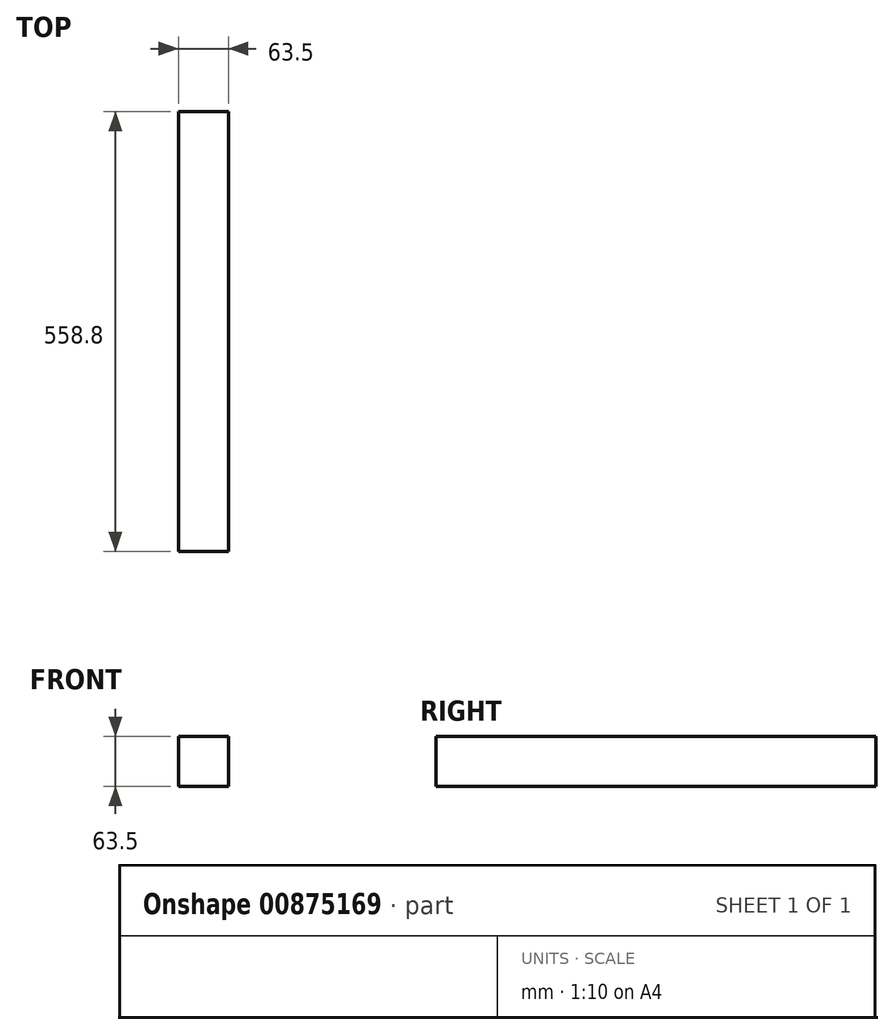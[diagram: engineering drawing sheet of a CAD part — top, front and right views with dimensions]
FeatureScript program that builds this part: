
annotation { "Feature Type Name" : "Feature", "Feature Type Description" : "" }
export const myFeature = defineFeature(function(context is Context, id is Id, definition is map)
    precondition{}
    {
        {
            var Q0;
            Q0=qCreatedBy(makeId("Front.planeOp"),FACE);
            var sketch = newSketch(context, id + "F0", { "sketchPlane" : qUnion([Q0])});
            skLineSegment(sketch, "E0.bottom", {"start": v(-164.57, 68.12) * mm, "end": v(-101.07, 68.12) * mm});
            skLineSegment(sketch, "E0.top", {"start": v(-164.57, 4.62) * mm, "end": v(-101.07, 4.62) * mm});
            skLineSegment(sketch, "E0.left", {"start": v(-164.57, 68.12) * mm, "end": v(-164.57, 4.62) * mm});
            skLineSegment(sketch, "E0.right", {"start": v(-101.07, 68.12) * mm, "end": v(-101.07, 4.62) * mm});
            skSolve(sketch);
        }
        {
            var Q0;
            Q0=makeQuery(id+"F0.imprint","IMPRINT",FACE,{"disambiguationData":[TD([[makeQuery(id+"F0.imprint","IMPRINT",EDGE,{"derivedFrom":sQuery(id+"F0.wireOp",EDGE,"E0.bottom")}),-1.0]])]});
            extrude(context, id + "F1", {"entities" : qUnion([Q0]), "depth" : 1498.6 * mm, "offsetDistance" : 25.4 * mm});
        }
        {
            var Q0;
            Q0=makeQuery(id+"F1.opExtrude","CAP_FACE",FACE,{"disambiguationData":[OSD([sQuery(id+"F0.wireOp",EDGE,"E0.bottom"),sQuery(id+"F0.wireOp",EDGE,"E0.top"),sQuery(id+"F0.wireOp",EDGE,"E0.left"),sQuery(id+"F0.wireOp",EDGE,"E0.right")])],"isStart":true});
            extrude(context, id + "F2", {"entities" : qUnion([Q0]), "operationType" : NewBodyOperationType.REMOVE, "oppositeDirection" : true, "depth" : 1092.2 * mm, "offsetDistance" : 25.4 * mm});
        }
        {
            var Q0;
            Q0=makeQuery(id+"F2.boolean.opBoolean","COPY",FACE,{"derivedFrom":makeQuery(id+"F2.opExtrude","CAP_FACE",FACE,{"disambiguationData":[OSD([sQuery(id+"F0.wireOp",EDGE,"E0.bottom"),sQuery(id+"F0.wireOp",EDGE,"E0.top"),sQuery(id+"F0.wireOp",EDGE,"E0.left"),sQuery(id+"F0.wireOp",EDGE,"E0.right")])],"isStart":false})});
            extrude(context, id + "F3", {"entities" : qUnion([Q0]), "operationType" : NewBodyOperationType.REMOVE, "oppositeDirection" : true, "depth" : 203.2 * mm, "offsetDistance" : 25.4 * mm});
        }
        {
            var Q0;
            Q0=makeQuery(id+"F1.opExtrude","CAP_FACE",FACE,{"disambiguationData":[OSD([sQuery(id+"F0.wireOp",EDGE,"E0.bottom"),sQuery(id+"F0.wireOp",EDGE,"E0.top"),sQuery(id+"F0.wireOp",EDGE,"E0.left"),sQuery(id+"F0.wireOp",EDGE,"E0.right")])],"isStart":false});
            extrude(context, id + "F4", {"entities" : qUnion([Q0]), "operationType" : NewBodyOperationType.REMOVE, "oppositeDirection" : true, "depth" : 177.8 * mm, "offsetDistance" : 25.4 * mm});
        }
        {
            var Q0;
            Q0=makeQuery(id+"F3.boolean.opBoolean","COPY",FACE,{"derivedFrom":makeQuery(id+"F3.opExtrude","CAP_FACE",FACE,{"disambiguationData":[OSD([sQuery(id+"F0.wireOp",EDGE,"E0.bottom"),sQuery(id+"F0.wireOp",EDGE,"E0.top"),sQuery(id+"F0.wireOp",EDGE,"E0.left"),sQuery(id+"F0.wireOp",EDGE,"E0.right")])],"isStart":false})});
            extrude(context, id + "F5", {"entities" : qUnion([Q0]), "operationType" : NewBodyOperationType.ADD, "depth" : 279.4 * mm, "offsetDistance" : 25.4 * mm});
        }
        {
            var Q0;
            Q0=makeQuery(id+"F5.opExtrude","CAP_FACE",FACE,{"disambiguationData":[OSD([sQuery(id+"F0.wireOp",EDGE,"E0.bottom"),sQuery(id+"F0.wireOp",EDGE,"E0.top"),sQuery(id+"F0.wireOp",EDGE,"E0.left"),sQuery(id+"F0.wireOp",EDGE,"E0.right")])],"isStart":false});
            extrude(context, id + "F6", {"entities" : qUnion([Q0]), "operationType" : NewBodyOperationType.ADD, "depth" : 254 * mm, "offsetDistance" : 25.4 * mm});
        }
        {
            var Q0;
            Q0=makeQuery(id+"F6.opExtrude","CAP_FACE",FACE,{"disambiguationData":[OSD([sQuery(id+"F0.wireOp",EDGE,"E0.bottom"),sQuery(id+"F0.wireOp",EDGE,"E0.top"),sQuery(id+"F0.wireOp",EDGE,"E0.left"),sQuery(id+"F0.wireOp",EDGE,"E0.right")])],"isStart":false});
            extrude(context, id + "F7", {"entities" : qUnion([Q0]), "operationType" : NewBodyOperationType.REMOVE, "oppositeDirection" : true, "depth" : 25.4 * mm, "offsetDistance" : 25.4 * mm});
        }
        {
            var Q0;
            Q0=makeQuery(id+"F7.boolean.opBoolean","COPY",FACE,{"derivedFrom":makeQuery(id+"F7.opExtrude","CAP_FACE",FACE,{"disambiguationData":[OSD([sQuery(id+"F0.wireOp",EDGE,"E0.bottom"),sQuery(id+"F0.wireOp",EDGE,"E0.top"),sQuery(id+"F0.wireOp",EDGE,"E0.left"),sQuery(id+"F0.wireOp",EDGE,"E0.right")])],"isStart":false})});
            extrude(context, id + "F8", {"entities" : qUnion([Q0]), "operationType" : NewBodyOperationType.ADD, "depth" : 12.7 * mm, "offsetDistance" : 25.4 * mm});
        }
        {
            var Q0;
            Q0=makeQuery(id+"F8.opExtrude","CAP_FACE",FACE,{"disambiguationData":[OSD([sQuery(id+"F0.wireOp",EDGE,"E0.bottom"),sQuery(id+"F0.wireOp",EDGE,"E0.top"),sQuery(id+"F0.wireOp",EDGE,"E0.left"),sQuery(id+"F0.wireOp",EDGE,"E0.right")])],"isStart":false});
            extrude(context, id + "F9", {"entities" : qUnion([Q0]), "operationType" : NewBodyOperationType.REMOVE, "oppositeDirection" : true, "depth" : 12.7 * mm, "offsetDistance" : 25.4 * mm});
        }
        {
            var Q0;
            Q0=makeQuery(id+"F9.boolean.opBoolean","COPY",FACE,{"derivedFrom":makeQuery(id+"F9.opExtrude","CAP_FACE",FACE,{"disambiguationData":[OSD([sQuery(id+"F0.wireOp",EDGE,"E0.bottom"),sQuery(id+"F0.wireOp",EDGE,"E0.top"),sQuery(id+"F0.wireOp",EDGE,"E0.left"),sQuery(id+"F0.wireOp",EDGE,"E0.right")])],"isStart":false})});
            extrude(context, id + "F10", {"entities" : qUnion([Q0]), "operationType" : NewBodyOperationType.REMOVE, "oppositeDirection" : true, "depth" : 12.7 * mm, "offsetDistance" : 25.4 * mm});
        }
        {
            var Q0;
            Q0=makeQuery(id+"F4.boolean.opBoolean","COPY",FACE,{"derivedFrom":makeQuery(id+"F4.opExtrude","CAP_FACE",FACE,{"disambiguationData":[OSD([sQuery(id+"F0.wireOp",EDGE,"E0.bottom"),sQuery(id+"F0.wireOp",EDGE,"E0.top"),sQuery(id+"F0.wireOp",EDGE,"E0.left"),sQuery(id+"F0.wireOp",EDGE,"E0.right")])],"isStart":false})});
            extrude(context, id + "F11", {"entities" : qUnion([Q0]), "operationType" : NewBodyOperationType.ADD, "depth" : 38.1 * mm, "offsetDistance" : 25.4 * mm});
        }
    });
